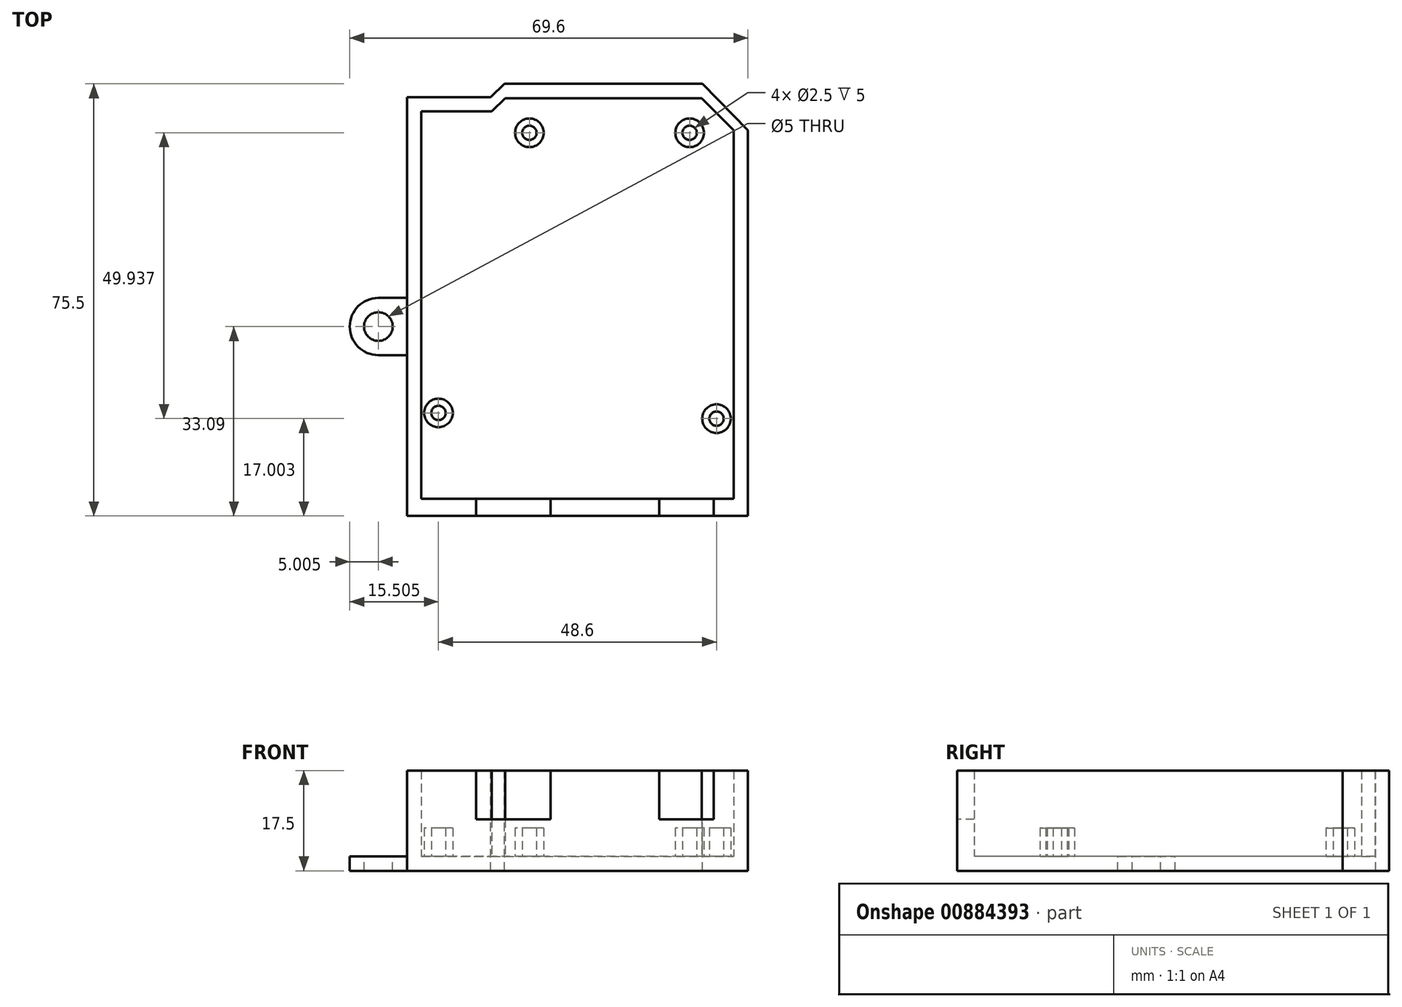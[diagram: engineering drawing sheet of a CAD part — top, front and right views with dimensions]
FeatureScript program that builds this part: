
annotation { "Feature Type Name" : "Feature", "Feature Type Description" : "" }
export const myFeature = defineFeature(function(context is Context, id is Id, definition is map)
    precondition{}
    {
        {
            var Q0;
            Q0=qCreatedBy(makeId("Top.planeOp"),FACE);
            var sketch = newSketch(context, id + "F0", { "sketchPlane" : qUnion([Q0])});
            skLineSegment(sketch, "E0", {"start": v(27.01, 34.31) * mm, "end": v(27.01, -30.09) * mm});
            skLineSegment(sketch, "E1", {"start": v(27.01, -30.09) * mm, "end": v(-27.59, -30.09) * mm});
            skLineSegment(sketch, "E2", {"start": v(-27.59, 37.59) * mm, "end": v(-27.59, -30.09) * mm});
            skCircle(sketch, "E3", {"center": v(-8.69, 33.85) * mm, "radius": 2.5 * mm});
            skCircle(sketch, "E4", {"center": v(19.31, 33.85) * mm, "radius": 2.5 * mm});
            skCircle(sketch, "E5", {"center": v(-8.69, 33.85) * mm, "radius": 1.25 * mm});
            skCircle(sketch, "E6", {"center": v(19.31, 33.85) * mm, "radius": 1.25 * mm});
            skCircle(sketch, "E7", {"center": v(24.01, -16.09) * mm, "radius": 2.5 * mm});
            skCircle(sketch, "E8", {"center": v(-24.59, -15.09) * mm, "radius": 2.5 * mm});
            skCircle(sketch, "E9", {"center": v(24.01, -16.09) * mm, "radius": 1.25 * mm});
            skCircle(sketch, "E10", {"center": v(-24.59, -15.09) * mm, "radius": 1.25 * mm});
            skLineSegment(sketch, "E11", {"start": v(-27.59, 37.59) * mm, "end": v(-15.24, 37.59) * mm});
            skLineSegment(sketch, "E12", {"start": v(-15.24, 37.59) * mm, "end": v(-12.92, 39.91) * mm});
            skLineSegment(sketch, "E13", {"start": v(21.41, 39.91) * mm, "end": v(27.01, 34.31) * mm});
            skLineSegment(sketch, "E14", {"start": v(-12.92, 39.91) * mm, "end": v(21.41, 39.91) * mm});
            skLineSegment(sketch, "E15", {"start": v(-27.59, -30.09) * mm, "end": v(-30.09, -30.09) * mm});
            skLineSegment(sketch, "E16", {"start": v(-30.09, -30.09) * mm, "end": v(-30.09, 40.09) * mm});
            skLineSegment(sketch, "E17", {"start": v(-30.09, 40.09) * mm, "end": v(-15.47, 40.09) * mm});
            skLineSegment(sketch, "E18", {"start": v(-15.47, 40.09) * mm, "end": v(-13.07, 42.41) * mm});
            skLineSegment(sketch, "E19", {"start": v(-13.07, 42.41) * mm, "end": v(21.57, 42.41) * mm});
            skLineSegment(sketch, "E20", {"start": v(27.01, -30.09) * mm, "end": v(29.51, -30.09) * mm});
            skLineSegment(sketch, "E21", {"start": v(29.51, -30.09) * mm, "end": v(29.51, 34.31) * mm});
            skLineSegment(sketch, "E22", {"start": v(29.51, 34.31) * mm, "end": v(21.57, 42.41) * mm});
            skLineSegment(sketch, "E23", {"start": v(-30.09, -33.09) * mm, "end": v(29.51, -33.09) * mm});
            skLineSegment(sketch, "E24", {"start": v(29.51, -33.09) * mm, "end": v(29.51, -30.09) * mm});
            skLineSegment(sketch, "E25", {"start": v(-30.09, -33.09) * mm, "end": v(-30.09, -30.09) * mm});
            skLineSegment(sketch, "E26", {"start": v(23.51, -33.09) * mm, "end": v(23.51, -30.09) * mm});
            skLineSegment(sketch, "E27", {"start": v(14.01, -30.09) * mm, "end": v(14.01, -33.09) * mm});
            skLineSegment(sketch, "E28", {"start": v(-4.99, -30.09) * mm, "end": v(-4.99, -33.09) * mm});
            skLineSegment(sketch, "E29", {"start": v(-17.99, -30.09) * mm, "end": v(-17.99, -33.09) * mm});
            skLineSegment(sketch, "E30.left", {"start": v(-30.09, 0) * mm, "end": v(-30.09, 10) * mm});
            skLineSegment(sketch, "E31", {"start": v(0, 0) * mm, "end": v(-56.03, 0) * mm, "construction": true});
            skLineSegment(sketch, "E32", {"start": v(-30.09, 0) * mm, "end": v(-44.37, 0) * mm, "construction": true});
            skLineSegment(sketch, "E33", {"start": v(-30.09, 5) * mm, "end": v(-35.09, 5) * mm});
            skLineSegment(sketch, "E34", {"start": v(-40.09, 0) * mm, "end": v(-40.09, 0) * mm});
            skLineSegment(sketch, "E35", {"start": v(-35.09, -5) * mm, "end": v(-30.09, -5) * mm});
            skPoint(sketch, "E36.visualSharp", {"position": v(-40.09, 5) * mm});
            skArc(sketch, "E36.filletArc", {"start": v(-35.09, 5) * mm, "mid": v(-38.62, 3.54) * mm, "end": v(-40.09, 0) * mm});
            skPoint(sketch, "E37.visualSharp", {"position": v(-40.09, -5) * mm});
            skArc(sketch, "E37.filletArc", {"start": v(-40.09, 0) * mm, "mid": v(-38.62, -3.54) * mm, "end": v(-35.09, -5) * mm});
            skCircle(sketch, "E38", {"center": v(-35.09, 0) * mm, "radius": 2.5 * mm});
            skSolve(sketch);
        }
        {
            var Q0;
            {var subQ0=sQuery(id+"F0.wireOp",EDGE,"E26");Q0=makeQuery(id+"F0.imprint","IMPRINT",FACE,{"disambiguationData":[TD([[makeQuery(id+"F0.imprint","IMPRINT",EDGE,{"derivedFrom":subQ0}),1.0]])]});}
            var Q1;
            {var subQ3=sQuery(id+"F0.wireOp",EDGE,"E15");Q1=makeQuery(id+"F0.imprint","IMPRINT",FACE,{"disambiguationData":[TD([[makeQuery(id+"F0.imprint","IMPRINT",EDGE,{"derivedFrom":subQ3}),1.0]])]});}
            var Q2;
            Q2=makeQuery(id+"F0.imprint","IMPRINT",FACE,{"disambiguationData":[TD([[makeQuery(id+"F0.imprint","IMPRINT",EDGE,{"derivedFrom":sQuery(id+"F0.wireOp",EDGE,"E4")}),1.0]])]});
            var Q3;
            {var subQ3=sQuery(id+"F0.wireOp",EDGE,"E20");Q3=makeQuery(id+"F0.imprint","IMPRINT",FACE,{"disambiguationData":[TD([[makeQuery(id+"F0.imprint","IMPRINT",EDGE,{"derivedFrom":subQ3}),-1.0]])]});}
            var Q4;
            {var subQ0=sQuery(id+"F0.wireOp",EDGE,"E27");Q4=makeQuery(id+"F0.imprint","IMPRINT",FACE,{"disambiguationData":[TD([[makeQuery(id+"F0.imprint","IMPRINT",EDGE,{"derivedFrom":subQ0}),-1.0]])]});}
            var Q5;
            Q5=makeQuery(id+"F0.imprint","IMPRINT",FACE,{"disambiguationData":[TD([[makeQuery(id+"F0.imprint","IMPRINT",EDGE,{"derivedFrom":sQuery(id+"F0.wireOp",EDGE,"E30.bottom")}),-1.0]])]});
            var Q6;
            {var subQ0=sQuery(id+"F0.wireOp",EDGE,"E28");Q6=makeQuery(id+"F0.imprint","IMPRINT",FACE,{"disambiguationData":[TD([[makeQuery(id+"F0.imprint","IMPRINT",EDGE,{"derivedFrom":subQ0}),-1.0]])]});}
            var Q7;
            Q7=makeQuery(id+"F0.imprint","IMPRINT",FACE,{"disambiguationData":[TD([[makeQuery(id+"F0.imprint","IMPRINT",EDGE,{"derivedFrom":sQuery(id+"F0.wireOp",EDGE,"E8")}),1.0]])]});
            var Q8;
            Q8=makeQuery(id+"F0.imprint","IMPRINT",FACE,{"disambiguationData":[TD([[makeQuery(id+"F0.imprint","IMPRINT",EDGE,{"derivedFrom":sQuery(id+"F0.wireOp",EDGE,"E7")}),1.0]])]});
            var Q9;
            Q9=makeQuery(id+"F0.imprint","IMPRINT",FACE,{"disambiguationData":[TD([[makeQuery(id+"F0.imprint","IMPRINT",EDGE,{"derivedFrom":sQuery(id+"F0.wireOp",EDGE,"E0")}),1.0]])]});
            var Q10;
            Q10=makeQuery(id+"F0.imprint","IMPRINT",FACE,{"disambiguationData":[TD([[makeQuery(id+"F0.imprint","IMPRINT",EDGE,{"derivedFrom":sQuery(id+"F0.wireOp",EDGE,"E3")}),1.0]])]});
            var Q11;
            {var subQ4=sQuery(id+"F0.wireOp",EDGE,"E0");Q11=makeQuery(id+"F0.imprint","IMPRINT",FACE,{"disambiguationData":[TD([[makeQuery(id+"F0.imprint","IMPRINT",EDGE,{"derivedFrom":subQ4}),-1.0]])]});}
            var Q12;
            Q12=makeQuery(id+"F0.imprint","IMPRINT",FACE,{"disambiguationData":[TD([[makeQuery(id+"F0.imprint","IMPRINT",EDGE,{"derivedFrom":sQuery(id+"F0.wireOp",EDGE,"E10")}),1.0]])]});
            var Q13;
            Q13=makeQuery(id+"F0.imprint","IMPRINT",FACE,{"disambiguationData":[TD([[makeQuery(id+"F0.imprint","IMPRINT",EDGE,{"derivedFrom":sQuery(id+"F0.wireOp",EDGE,"E9")}),1.0]])]});
            var Q14;
            Q14=makeQuery(id+"F0.imprint","IMPRINT",FACE,{"disambiguationData":[TD([[makeQuery(id+"F0.imprint","IMPRINT",EDGE,{"derivedFrom":sQuery(id+"F0.wireOp",EDGE,"E5")}),1.0]])]});
            var Q15;
            Q15=makeQuery(id+"F0.imprint","IMPRINT",FACE,{"disambiguationData":[TD([[makeQuery(id+"F0.imprint","IMPRINT",EDGE,{"derivedFrom":sQuery(id+"F0.wireOp",EDGE,"E6")}),1.0]])]});
            extrude(context, id + "F1", {"entities" : qUnion([Q0, Q1, Q2, Q3, Q4, Q5, Q6, Q7, Q8, Q9, Q10, Q11, Q12, Q13, Q14, Q15]), "oppositeDirection" : true, "depth" : 2.5 * mm, "offsetDistance" : 25 * mm});
        }
        {
            var Q0;
            Q0=makeQuery(id+"F0.imprint","IMPRINT",FACE,{"disambiguationData":[TD([[makeQuery(id+"F0.imprint","IMPRINT",EDGE,{"derivedFrom":sQuery(id+"F0.wireOp",EDGE,"E0")}),1.0]])]});
            var Q1;
            {var subQ3=sQuery(id+"F0.wireOp",EDGE,"E15");Q1=makeQuery(id+"F0.imprint","IMPRINT",FACE,{"disambiguationData":[TD([[makeQuery(id+"F0.imprint","IMPRINT",EDGE,{"derivedFrom":subQ3}),1.0]])]});}
            var Q2;
            {var subQ0=sQuery(id+"F0.wireOp",EDGE,"E27");Q2=makeQuery(id+"F0.imprint","IMPRINT",FACE,{"disambiguationData":[TD([[makeQuery(id+"F0.imprint","IMPRINT",EDGE,{"derivedFrom":subQ0}),-1.0]])]});}
            var Q3;
            {var subQ3=sQuery(id+"F0.wireOp",EDGE,"E20");Q3=makeQuery(id+"F0.imprint","IMPRINT",FACE,{"disambiguationData":[TD([[makeQuery(id+"F0.imprint","IMPRINT",EDGE,{"derivedFrom":subQ3}),-1.0]])]});}
            extrude(context, id + "F2", {"entities" : qUnion([Q0, Q1, Q2, Q3]), "operationType" : NewBodyOperationType.ADD, "depth" : 15 * mm, "offsetDistance" : 25 * mm});
        }
        {
            var Q0;
            {var subQ0=sQuery(id+"F0.wireOp",EDGE,"E28");Q0=makeQuery(id+"F0.imprint","IMPRINT",FACE,{"disambiguationData":[TD([[makeQuery(id+"F0.imprint","IMPRINT",EDGE,{"derivedFrom":subQ0}),-1.0]])]});}
            var Q1;
            {var subQ0=sQuery(id+"F0.wireOp",EDGE,"E26");Q1=makeQuery(id+"F0.imprint","IMPRINT",FACE,{"disambiguationData":[TD([[makeQuery(id+"F0.imprint","IMPRINT",EDGE,{"derivedFrom":subQ0}),1.0]])]});}
            extrude(context, id + "F3", {"entities" : qUnion([Q0, Q1]), "operationType" : NewBodyOperationType.ADD, "depth" : 6.5 * mm, "offsetDistance" : 25 * mm});
        }
        {
            var Q0;
            {var subQ4=sQuery(id+"F0.wireOp",EDGE,"E33");Q0=makeQuery(id+"F0.imprint","IMPRINT",FACE,{"disambiguationData":[TD([[makeQuery(id+"F0.imprint","IMPRINT",EDGE,{"derivedFrom":subQ4}),1.0]])]});}
            extrude(context, id + "F4", {"entities" : qUnion([Q0]), "operationType" : NewBodyOperationType.ADD, "oppositeDirection" : true, "depth" : 2.5 * mm, "offsetDistance" : 25 * mm});
        }
        {
            var Q0;
            Q0=makeQuery(id+"F0.imprint","IMPRINT",FACE,{"disambiguationData":[TD([[makeQuery(id+"F0.imprint","IMPRINT",EDGE,{"derivedFrom":sQuery(id+"F0.wireOp",EDGE,"E8")}),1.0]])]});
            var Q1;
            Q1=makeQuery(id+"F0.imprint","IMPRINT",FACE,{"disambiguationData":[TD([[makeQuery(id+"F0.imprint","IMPRINT",EDGE,{"derivedFrom":sQuery(id+"F0.wireOp",EDGE,"E3")}),1.0]])]});
            var Q2;
            Q2=makeQuery(id+"F0.imprint","IMPRINT",FACE,{"disambiguationData":[TD([[makeQuery(id+"F0.imprint","IMPRINT",EDGE,{"derivedFrom":sQuery(id+"F0.wireOp",EDGE,"E4")}),1.0]])]});
            var Q3;
            Q3=makeQuery(id+"F0.imprint","IMPRINT",FACE,{"disambiguationData":[TD([[makeQuery(id+"F0.imprint","IMPRINT",EDGE,{"derivedFrom":sQuery(id+"F0.wireOp",EDGE,"E7")}),1.0]])]});
            extrude(context, id + "F5", {"entities" : qUnion([Q0, Q1, Q2, Q3]), "operationType" : NewBodyOperationType.ADD, "depth" : 5 * mm, "offsetDistance" : 25 * mm});
        }
    });
